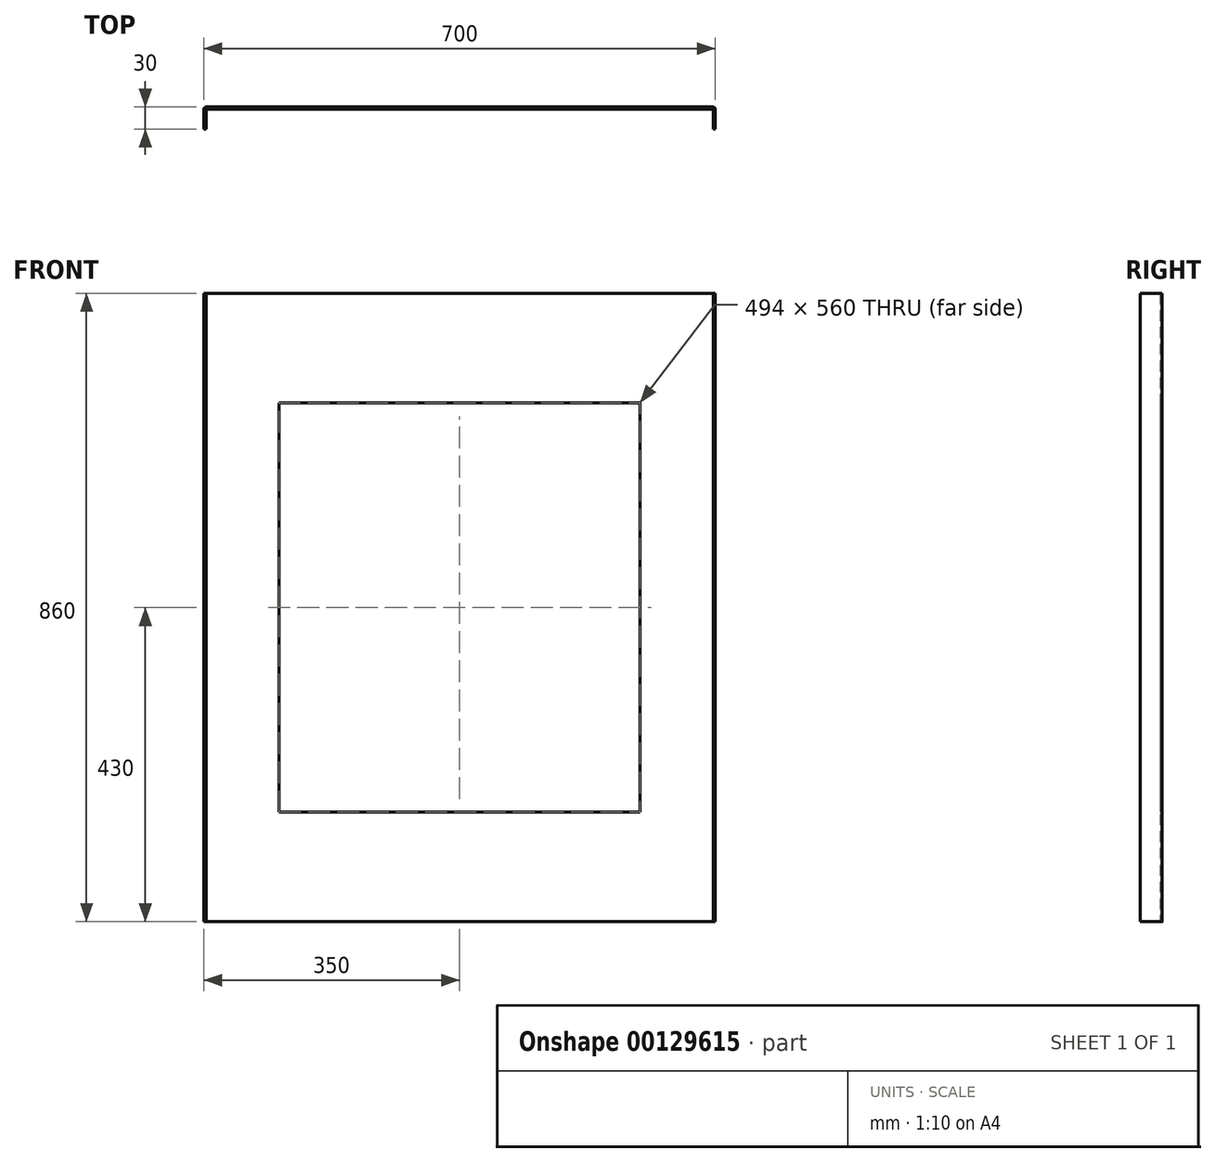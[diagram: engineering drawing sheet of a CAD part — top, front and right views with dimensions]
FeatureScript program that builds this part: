
annotation { "Feature Type Name" : "Feature", "Feature Type Description" : "" }
export const myFeature = defineFeature(function(context is Context, id is Id, definition is map)
    precondition{}
    {
        {
            var Q0;
            Q0=qCreatedBy(makeId("Top.planeOp"),FACE);
            var sketch = newSketch(context, id + "F0", { "sketchPlane" : qUnion([Q0])});
            skLineSegment(sketch, "E0", {"start": v(0, 0) * mm, "end": v(0, 3) * mm, "construction": true});
            skLineSegment(sketch, "E1", {"start": v(0, 3) * mm, "end": v(-347, 3) * mm});
            skLineSegment(sketch, "E2", {"start": v(0, 3) * mm, "end": v(347, 3) * mm});
            skLineSegment(sketch, "E3", {"start": v(350, 0) * mm, "end": v(350, -27) * mm});
            skLineSegment(sketch, "E4", {"start": v(350, -27) * mm, "end": v(347, -27) * mm});
            skLineSegment(sketch, "E5", {"start": v(347, -27) * mm, "end": v(347, -1.5) * mm});
            skLineSegment(sketch, "E6.MirrorCS", {"start": v(-350, -27) * mm, "end": v(-347, -27) * mm});
            skLineSegment(sketch, "E7.MirrorCS", {"start": v(-347, -27) * mm, "end": v(-347, -1.5) * mm});
            skLineSegment(sketch, "E8.MirrorCS", {"start": v(-350, 0) * mm, "end": v(-350, -27) * mm});
            skPoint(sketch, "E9.visualSharp", {"position": v(-347, 0) * mm});
            skArc(sketch, "E9.filletArc", {"start": v(-345.5, 0) * mm, "mid": v(-346.56, -0.44) * mm, "end": v(-347, -1.5) * mm});
            skPoint(sketch, "E10.visualSharp", {"position": v(-350, 3) * mm});
            skArc(sketch, "E10.filletArc", {"start": v(-347, 3) * mm, "mid": v(-349.12, 2.12) * mm, "end": v(-350, 0) * mm});
            skPoint(sketch, "E11.visualSharp", {"position": v(350, 3) * mm});
            skArc(sketch, "E11.filletArc", {"start": v(350, 0) * mm, "mid": v(349.12, 2.12) * mm, "end": v(347, 3) * mm});
            skArc(sketch, "E12.filletArc", {"start": v(347, -1.5) * mm, "mid": v(346.56, -0.44) * mm, "end": v(345.5, 0) * mm});
            skLineSegment(sketch, "E13", {"start": v(350, -27) * mm, "end": v(-350, -27) * mm, "construction": true});
            skLineSegment(sketch, "E14", {"start": v(-345.5, 0) * mm, "end": v(345.5, 0) * mm});
            skSolve(sketch);
        }
        {
            var Q0;
            Q0=makeQuery(id+"F0.imprint","IMPRINT",FACE,{"disambiguationData":[TD([[makeQuery(id+"F0.imprint","IMPRINT",EDGE,{"derivedFrom":sQuery(id+"F0.wireOp",EDGE,"E1")}),1.0]])]});
            extrude(context, id + "F1", {"entities" : qUnion([Q0]), "depth" : 860 * mm});
        }
        {
            var Q0;
            Q0=makeQuery(id+"F1.opExtrude","SWEPT_FACE",FACE,{"disambiguationData":[OSD([sQuery(id+"F0.wireOp",EDGE,"E14")])]});
            var sketch = newSketch(context, id + "F2", { "sketchPlane" : qUnion([Q0])});
            skLineSegment(sketch, "E15.bottom", {"start": v(-247, 710) * mm, "end": v(247, 710) * mm});
            skLineSegment(sketch, "E15.top", {"start": v(-247, 150) * mm, "end": v(247, 150) * mm});
            skLineSegment(sketch, "E15.left", {"start": v(-247, 710) * mm, "end": v(-247, 150) * mm});
            skLineSegment(sketch, "E15.right", {"start": v(247, 710) * mm, "end": v(247, 150) * mm});
            skSolve(sketch);
        }
        {
            var Q0;
            Q0=qSketchRegion(id+"F2",true);
            extrude(context, id + "F3", {"entities" : qUnion([Q0]), "operationType" : NewBodyOperationType.REMOVE, "oppositeDirection" : true, "depth" : 25 * mm});
        }
    });
